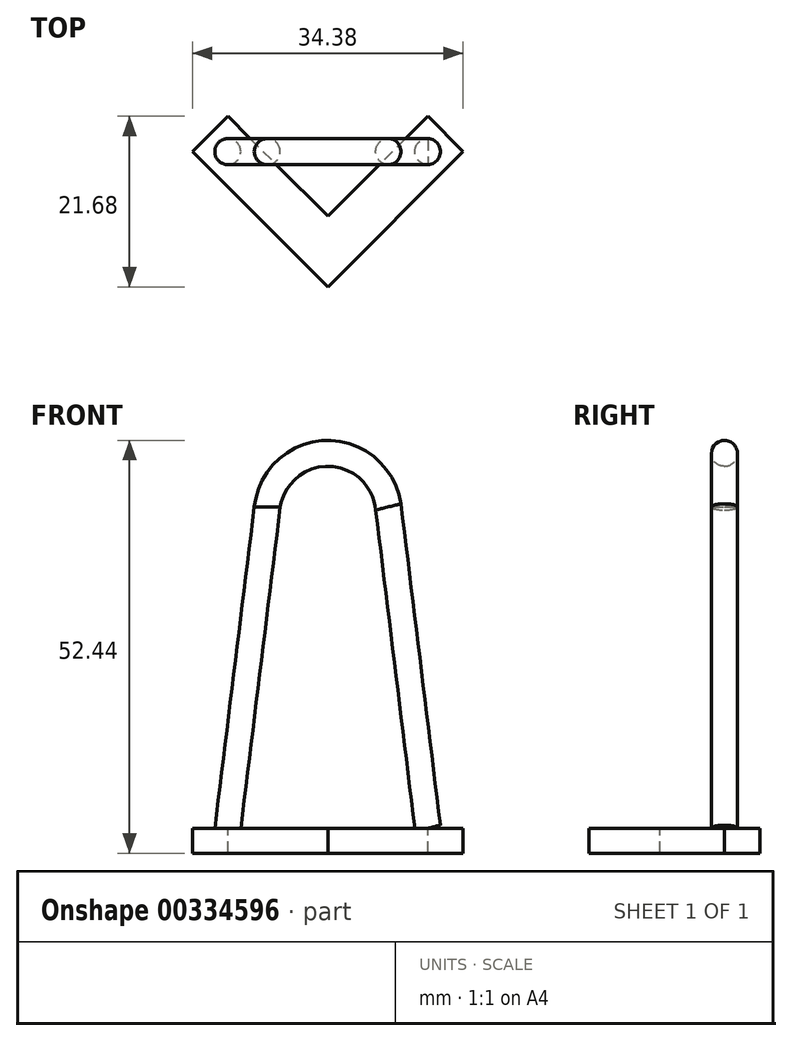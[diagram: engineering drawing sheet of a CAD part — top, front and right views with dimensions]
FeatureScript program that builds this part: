
annotation { "Feature Type Name" : "Feature", "Feature Type Description" : "" }
export const myFeature = defineFeature(function(context is Context, id is Id, definition is map)
    precondition{}
    {
        {
            var Q0;
            Q0=qCreatedBy(makeId("Front.planeOp"),FACE);
            var sketch = newSketch(context, id + "F0", { "sketchPlane" : qUnion([Q0])});
            skLineSegment(sketch, "E0", {"start": v(0, 0) * mm, "end": v(0, 47.63) * mm, "construction": true});
            skLineSegment(sketch, "E1", {"start": v(-12.7, 0) * mm, "end": v(12.7, 0) * mm, "construction": true});
            skLineSegment(sketch, "E2", {"start": v(-12.7, 0) * mm, "end": v(-7.69, 40.82) * mm});
            skLineSegment(sketch, "E3", {"start": v(12.7, 0) * mm, "end": v(7.69, 40.82) * mm});
            skArc(sketch, "E4", {"start": v(7.69, 40.82) * mm, "mid": v(0, 47.63) * mm, "end": v(-7.69, 40.82) * mm});
            skSolve(sketch);
        }
        {
            var Q0;
            Q0=qCreatedBy(makeId("Top.planeOp"),FACE);
            var sketch = newSketch(context, id + "F1", { "sketchPlane" : qUnion([Q0])});
            skCircle(sketch, "E5", {"center": v(-12.7, 0) * mm, "radius": 1.65 * mm});
            skSolve(sketch);
        }
        {
            var Q0;
            Q0=makeQuery(id+"F1.imprint","IMPRINT",FACE,{"disambiguationData":[TD([[makeQuery(id+"F1.imprint","IMPRINT",EDGE,{"derivedFrom":sQuery(id+"F1.wireOp",EDGE,"E5")}),1.0]])]});
            var Q1;
            Q1=sQuery(id+"F0.wireOp",EDGE,"E2");
            var Q2;
            Q2=sQuery(id+"F0.wireOp",EDGE,"E4");
            var Q3;
            Q3=sQuery(id+"F0.wireOp",EDGE,"E3");
            sweep(context, id + "F2", {"profiles" : qUnion([Q0]), "path" : qUnion([Q1, Q2, Q3])});
        }
        {
            var Q0;
            Q0=qCreatedBy(makeId("Top.planeOp"),FACE);
            var sketch = newSketch(context, id + "F3", { "sketchPlane" : qUnion([Q0])});
            skLineSegment(sketch, "E6", {"start": v(-12.7, 0) * mm, "end": v(12.7, 0) * mm, "construction": true});
            skLineSegment(sketch, "E7", {"start": v(0, 0) * mm, "end": v(0, -17.2) * mm, "construction": true});
            skLineSegment(sketch, "E8", {"start": v(0, -17.2) * mm, "end": v(-17.2, 0) * mm});
            skLineSegment(sketch, "E9", {"start": v(-17.2, 0) * mm, "end": v(-12.7, 4.5) * mm});
            skLineSegment(sketch, "E10", {"start": v(-12.7, 4.5) * mm, "end": v(0, -8.2) * mm});
            skLineSegment(sketch, "E11", {"start": v(0, -8.2) * mm, "end": v(0, -17.2) * mm});
            skLineSegment(sketch, "E12.MirrorCS", {"start": v(0, -17.2) * mm, "end": v(17.2, 0) * mm});
            skLineSegment(sketch, "E13.MirrorCS", {"start": v(17.2, 0) * mm, "end": v(12.7, 4.5) * mm});
            skLineSegment(sketch, "E14.MirrorCS", {"start": v(12.7, 4.5) * mm, "end": v(0, -8.2) * mm});
            skSolve(sketch);
        }
        {
            var Q0;
            Q0=makeQuery(id+"F3.imprint","IMPRINT",FACE,{"disambiguationData":[TD([[makeQuery(id+"F3.imprint","IMPRINT",EDGE,{"derivedFrom":sQuery(id+"F3.wireOp",EDGE,"E8")}),-1.0]])]});
            var Q1;
            Q1=makeQuery(id+"F3.imprint","IMPRINT",FACE,{"disambiguationData":[TD([[makeQuery(id+"F3.imprint","IMPRINT",EDGE,{"derivedFrom":sQuery(id+"F3.wireOp",EDGE,"E11")}),1.0]])]});
            extrude(context, id + "F4", {"entities" : qUnion([Q0, Q1]), "operationType" : NewBodyOperationType.ADD, "oppositeDirection" : true, "depth" : 3.17 * mm});
        }
    });
